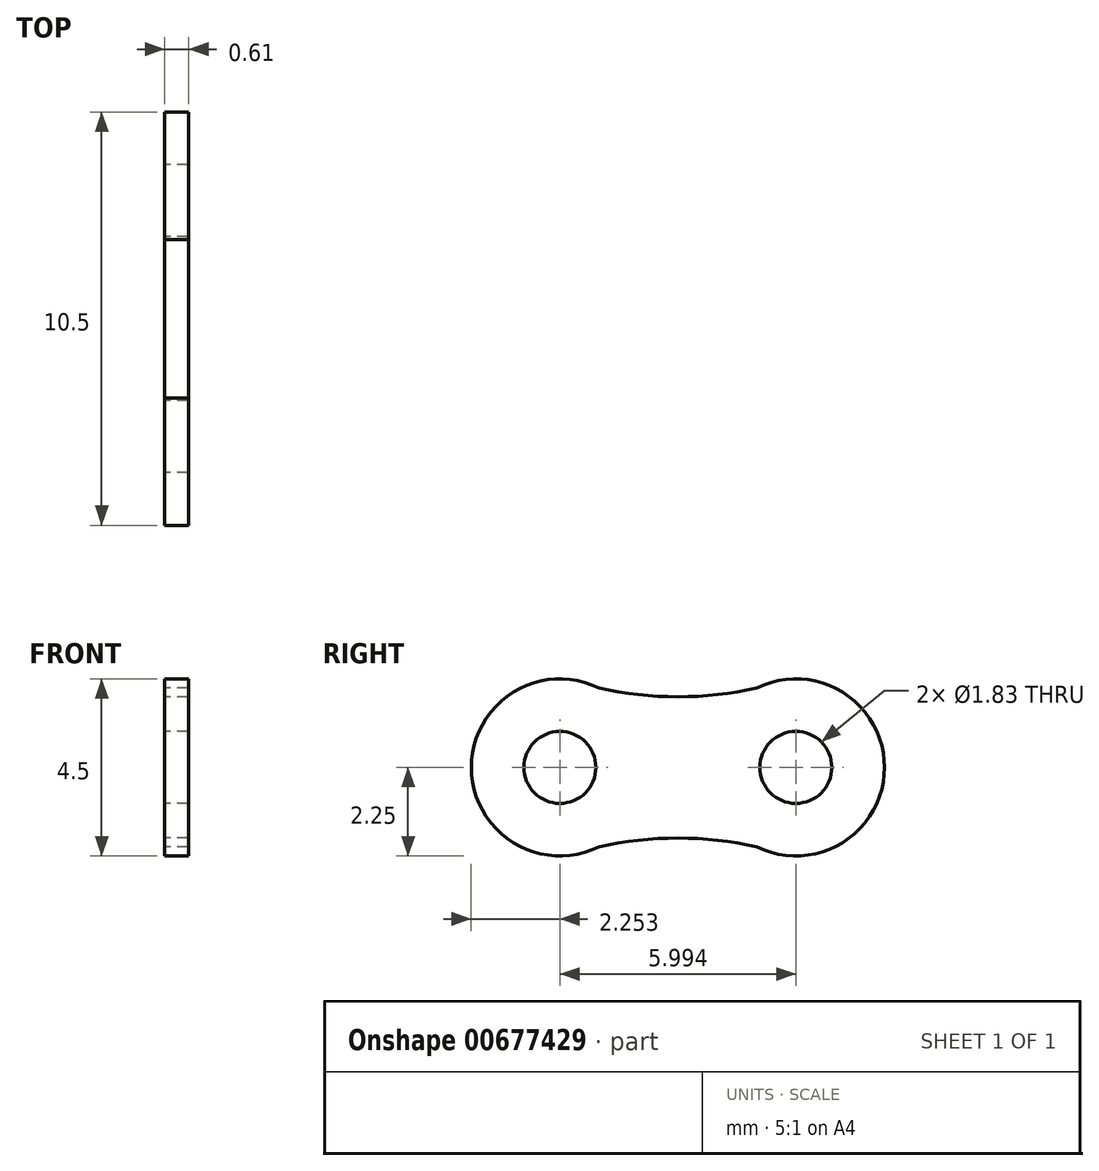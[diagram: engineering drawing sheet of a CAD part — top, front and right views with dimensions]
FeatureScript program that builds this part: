
annotation { "Feature Type Name" : "Feature", "Feature Type Description" : "" }
export const myFeature = defineFeature(function(context is Context, id is Id, definition is map)
    precondition{}
    {
        {
            var Q0;
            Q0=qCreatedBy(makeId("Right.planeOp"),FACE);
            var sketch = newSketch(context, id + "F0", { "sketchPlane" : qUnion([Q0])});
            skCircle(sketch, "E0", {"center": v(-3, 0) * mm, "radius": 0.91 * mm});
            skCircle(sketch, "E1.MirrorC", {"center": v(3, 0) * mm, "radius": 0.91 * mm});
            skArc(sketch, "E2", {"start": v(-2, 2.02) * mm, "mid": v(-5.25, 0) * mm, "end": v(-2, -2.02) * mm});
            skArc(sketch, "E3.MirrorC", {"start": v(2, 2.02) * mm, "mid": v(5.25, 0) * mm, "end": v(2, -2.02) * mm});
            skArc(sketch, "E4.0", {"start": v(-2, 2.02) * mm, "mid": v(0, 1.8) * mm, "end": v(2, 2.02) * mm});
            skArc(sketch, "E5.MirrorCS", {"start": v(-2, -2.02) * mm, "mid": v(0, -1.8) * mm, "end": v(2, -2.02) * mm});
            skSolve(sketch);
        }
        {
            var Q0;
            Q0 = qSketchRegion(id + "F0", true);
            extrude(context, id + "F1", {"entities" : qUnion([Q0]), "depth" : 0.6 * mm, "offsetDistance" : 25 * mm});
        }
    });
